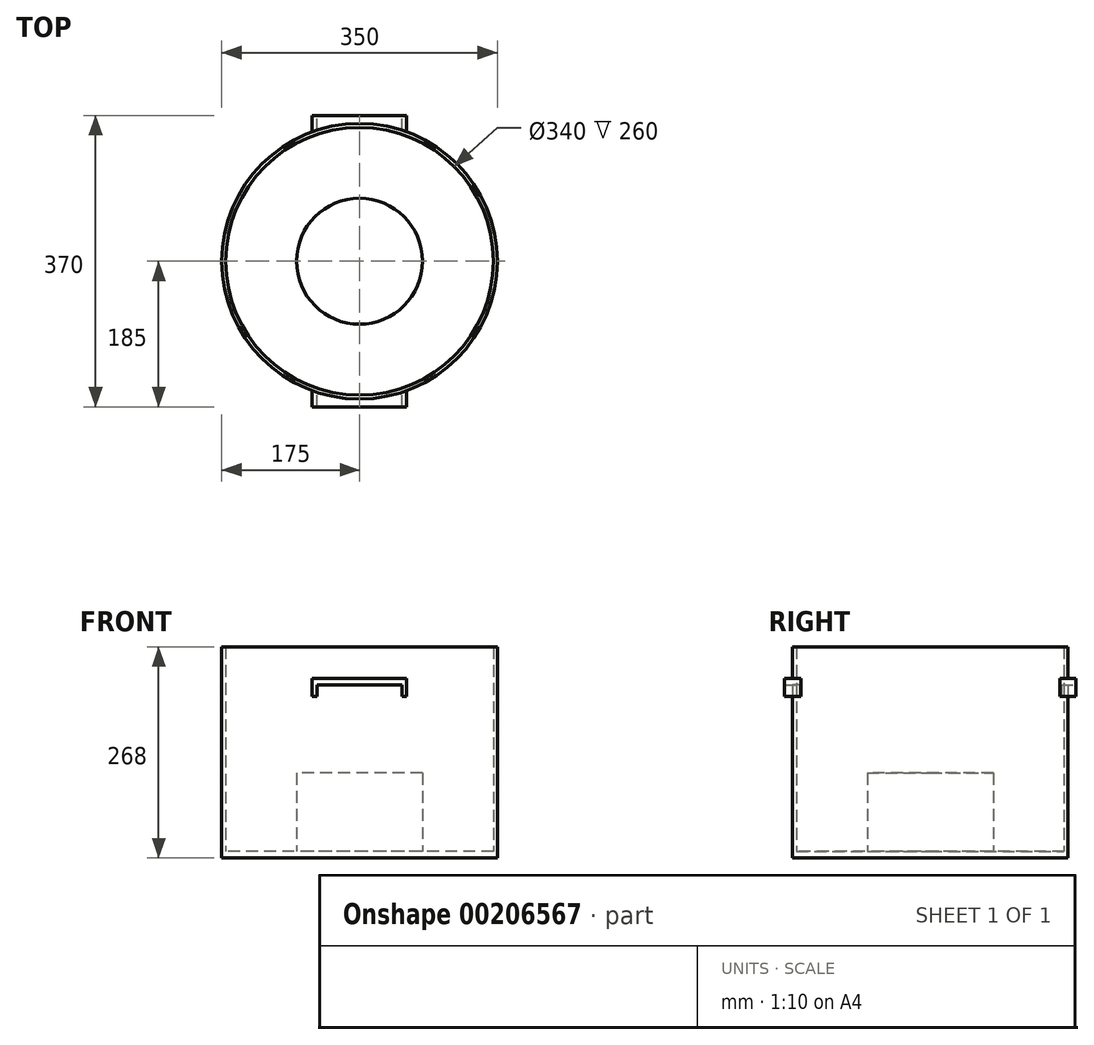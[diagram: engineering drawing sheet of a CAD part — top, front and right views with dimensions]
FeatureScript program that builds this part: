
annotation { "Feature Type Name" : "Feature", "Feature Type Description" : "" }
export const myFeature = defineFeature(function(context is Context, id is Id, definition is map)
    precondition{}
    {
        {
            var Q0;
            Q0=qCreatedBy(makeId("Top.planeOp"),FACE);
            var sketch = newSketch(context, id + "F0", { "sketchPlane" : qUnion([Q0])});
            skCircle(sketch, "E0", {"center": v(0, 0) * mm, "radius": 175 * mm});
            skSolve(sketch);
        }
        {
            var Q0;
            Q0 = qSketchRegion(id + "F0", true);
            extrude(context, id + "F1", {"entities" : qUnion([Q0]), "depth" : 8 * mm});
        }
        {
            var Q0;
            Q0=makeQuery(id+"F1.opExtrude","CAP_FACE",FACE,{"disambiguationData":[OSD([sQuery(id+"F0.wireOp",EDGE,"E0")])],"isStart":false});
            var sketch = newSketch(context, id + "F2", { "sketchPlane" : qUnion([Q0])});
            skCircle(sketch, "E1", {"center": v(0, 0) * mm, "radius": 175 * mm});
            skCircle(sketch, "E2", {"center": v(0, 0) * mm, "radius": 170 * mm});
            skSolve(sketch);
        }
        {
            var Q0;
            Q0 = qSketchRegion(id + "F2", true);
            extrude(context, id + "F3", {"entities" : qUnion([Q0]), "operationType" : NewBodyOperationType.ADD, "depth" : 260 * mm});
        }
        {
            var Q0;
            Q0=makeQuery(id+"F1.opExtrude","CAP_FACE",FACE,{"disambiguationData":[OSD([sQuery(id+"F0.wireOp",EDGE,"E0")])],"isStart":false});
            var sketch = newSketch(context, id + "F4", { "sketchPlane" : qUnion([Q0])});
            skCircle(sketch, "E3", {"center": v(0, 0) * mm, "radius": 80 * mm});
            skSolve(sketch);
        }
        {
            var Q0;
            Q0 = qSketchRegion(id + "F4", true);
            extrude(context, id + "F5", {"entities" : qUnion([Q0]), "operationType" : NewBodyOperationType.ADD, "depth" : 100 * mm});
        }
        {
            var Q0;
            Q0=qCreatedBy(makeId("Front.planeOp"),FACE);
            var sketch = newSketch(context, id + "F6", { "sketchPlane" : qUnion([Q0])});
            skLineSegment(sketch, "E4", {"start": v(0, 0) * mm, "end": v(0, 304.16) * mm});
            skLineSegment(sketch, "E5.bottom", {"start": v(-60, 228) * mm, "end": v(60, 228) * mm});
            skLineSegment(sketch, "E5.top", {"start": v(-60, 220) * mm, "end": v(60, 220) * mm});
            skLineSegment(sketch, "E5.left", {"start": v(-60, 228) * mm, "end": v(-60, 220) * mm});
            skLineSegment(sketch, "E5.right", {"start": v(60, 228) * mm, "end": v(60, 220) * mm});
            skPoint(sketch, "E5.middle", {"position": v(0, 224) * mm});
            skLineSegment(sketch, "E6.bottom", {"start": v(60, 220) * mm, "end": v(54, 220) * mm});
            skLineSegment(sketch, "E6.top", {"start": v(60, 205) * mm, "end": v(54, 205) * mm});
            skLineSegment(sketch, "E6.left", {"start": v(60, 220) * mm, "end": v(60, 205) * mm});
            skLineSegment(sketch, "E6.right", {"start": v(54, 220) * mm, "end": v(54, 205) * mm});
            skLineSegment(sketch, "E7.MirrorCS", {"start": v(-60, 205) * mm, "end": v(-54, 205) * mm});
            skLineSegment(sketch, "E8.MirrorCS", {"start": v(-54, 220) * mm, "end": v(-54, 205) * mm});
            skLineSegment(sketch, "E9.MirrorCS", {"start": v(-60, 220) * mm, "end": v(-60, 205) * mm});
            skSolve(sketch);
        }
        {
            var Q0;
            Q0 = qSketchRegion(id + "F6", true);
            extrude(context, id + "F7", {"entities" : qUnion([Q0]), "operationType" : NewBodyOperationType.ADD, "endBound" : BoundingType.SYMMETRIC, "depth" : 370 * mm});
        }
        {
            var Q0;
            Q0=makeQuery(id+"F3.opExtrude","CAP_FACE",FACE,{"disambiguationData":[OSD([sQuery(id+"F2.wireOp",EDGE,"E1"),sQuery(id+"F2.wireOp",EDGE,"E2")])],"isStart":false});
            var sketch = newSketch(context, id + "F8", { "sketchPlane" : qUnion([Q0])});
            skCircle(sketch, "E10", {"center": v(0, 0) * mm, "radius": 170 * mm});
            skSolve(sketch);
        }
        {
            var Q0;
            Q0 = qSketchRegion(id + "F8", true);
            extrude(context, id + "F9", {"entities" : qUnion([Q0]), "operationType" : NewBodyOperationType.REMOVE, "oppositeDirection" : true, "depth" : 100 * mm});
        }
    });
